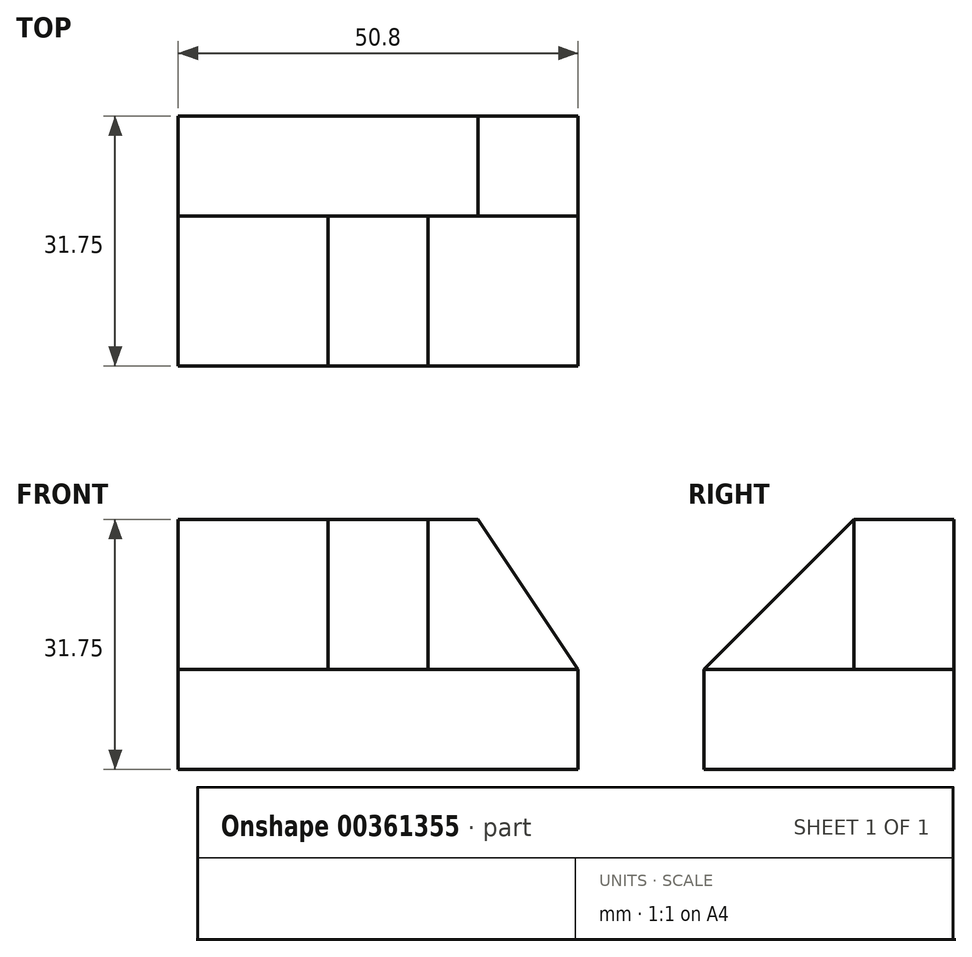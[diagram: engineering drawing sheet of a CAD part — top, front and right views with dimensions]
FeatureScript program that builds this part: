
annotation { "Feature Type Name" : "Feature", "Feature Type Description" : "" }
export const myFeature = defineFeature(function(context is Context, id is Id, definition is map)
    precondition{}
    {
        {
            var Q0;
            Q0=qCreatedBy(makeId("Right.planeOp"),FACE);
            var sketch = newSketch(context, id + "F0", { "sketchPlane" : qUnion([Q0])});
            skLineSegment(sketch, "E0", {"start": v(0, 0) * mm, "end": v(31.75, 0) * mm});
            skLineSegment(sketch, "E1", {"start": v(31.75, 0) * mm, "end": v(31.75, 31.75) * mm});
            skLineSegment(sketch, "E2", {"start": v(31.75, 31.75) * mm, "end": v(19.05, 31.75) * mm});
            skLineSegment(sketch, "E3", {"start": v(19.05, 31.75) * mm, "end": v(19.05, 12.7) * mm});
            skLineSegment(sketch, "E4", {"start": v(19.05, 12.7) * mm, "end": v(0, 12.7) * mm});
            skLineSegment(sketch, "E5", {"start": v(0, 12.7) * mm, "end": v(0, 0) * mm});
            skSolve(sketch);
        }
        {
            var Q0;
            Q0=makeQuery(id+"F0.imprint","IMPRINT",FACE,{"disambiguationData":[TD([[makeQuery(id+"F0.imprint","IMPRINT",EDGE,{"derivedFrom":sQuery(id+"F0.wireOp",EDGE,"E0")}),1.0]])]});
            extrude(context, id + "F1", {"entities" : qUnion([Q0]), "oppositeDirection" : true, "depth" : 50.8 * mm});
        }
        {
            var Q0;
            Q0=makeQuery(id+"F1.opExtrude","SWEPT_FACE",FACE,{"disambiguationData":[OSD([sQuery(id+"F0.wireOp",EDGE,"E3")])]});
            var sketch = newSketch(context, id + "F2", { "sketchPlane" : qUnion([Q0])});
            skLineSegment(sketch, "E6", {"start": v(-12.7, 31.75) * mm, "end": v(0, 12.7) * mm});
            skLineSegment(sketch, "E7", {"start": v(0, 12.7) * mm, "end": v(0, 31.75) * mm});
            skLineSegment(sketch, "E8", {"start": v(0, 31.75) * mm, "end": v(-12.7, 31.75) * mm});
            skSolve(sketch);
        }
        {
            var Q0;
            Q0=makeQuery(id+"F2.imprint","IMPRINT",FACE,{"disambiguationData":[TD([[makeQuery(id+"F2.imprint","IMPRINT",EDGE,{"derivedFrom":sQuery(id+"F2.wireOp",EDGE,"E6")}),1.0]])]});
            extrude(context, id + "F3", {"entities" : qUnion([Q0]), "operationType" : NewBodyOperationType.REMOVE, "oppositeDirection" : true, "depth" : 25.4 * mm});
        }
        {
            var Q0;
            Q0=makeQuery(id+"F1.opExtrude","SWEPT_FACE",FACE,{"disambiguationData":[OSD([sQuery(id+"F0.wireOp",EDGE,"E3")])]});
            var sketch = newSketch(context, id + "F4", { "sketchPlane" : qUnion([Q0])});
            skLineSegment(sketch, "E9", {"start": v(-50.8, 31.75) * mm, "end": v(-31.75, 31.75) * mm});
            skLineSegment(sketch, "E10", {"start": v(-31.75, 31.75) * mm, "end": v(-31.75, 12.7) * mm});
            skLineSegment(sketch, "E11", {"start": v(-31.75, 12.7) * mm, "end": v(-19.05, 12.7) * mm});
            skLineSegment(sketch, "E12", {"start": v(-19.05, 12.7) * mm, "end": v(-19.05, 31.75) * mm});
            skLineSegment(sketch, "E13", {"start": v(-19.05, 31.75) * mm, "end": v(-31.75, 31.75) * mm});
            skSolve(sketch);
        }
        {
            var Q0;
            Q0 = qSketchRegion(id + "F4", true);
            extrude(context, id + "F5", {"entities" : qUnion([Q0]), "operationType" : NewBodyOperationType.ADD, "depth" : 19.05 * mm});
        }
        {
            var Q0;
            Q0=makeQuery(id+"F5.opExtrude","SWEPT_FACE",FACE,{"disambiguationData":[OSD([sQuery(id+"F4.wireOp",EDGE,"E12")])]});
            var sketch = newSketch(context, id + "F6", { "sketchPlane" : qUnion([Q0])});
            skLineSegment(sketch, "E14", {"start": v(19.05, 31.75) * mm, "end": v(0, 12.7) * mm});
            skLineSegment(sketch, "E15", {"start": v(0, 12.7) * mm, "end": v(0, 31.75) * mm});
            skLineSegment(sketch, "E16", {"start": v(0, 31.75) * mm, "end": v(19.05, 31.75) * mm});
            skSolve(sketch);
        }
        {
            var Q0;
            Q0 = qSketchRegion(id + "F6", true);
            extrude(context, id + "F7", {"entities" : qUnion([Q0]), "operationType" : NewBodyOperationType.REMOVE, "oppositeDirection" : true, "depth" : 25.4 * mm});
        }
    });
